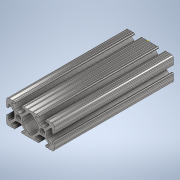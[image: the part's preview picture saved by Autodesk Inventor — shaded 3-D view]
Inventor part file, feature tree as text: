
AUTODESK INVENTOR PART (.ipt)
format: ipt  version: 2020 (Build 240168000, 168)  size: 343,552 bytes
history: native  units: in
note: dims shown in document units (in); Inventor stores cm internally (conversion verified against a paired STEP export)
features: sketch x2, extrude x1
ambient origin geometry x8: Origin, YZ Plane, XZ Plane, XY Plane, X Axis, Y Axis, Z Axis, Center Point
bodies: Solid1 (feature_tree)
feature tree (3):
  extrude  "Extrusion1"  [1 undecoded]
  sketch  "Sketch2"
  sketch  "Sketch1"  dims[d0=5.0in d1=0.0in]
note: 1 required parameter value undecoded (feature->parameter linkage not recoverable at this tier; creation-order binding heuristic only, values carry confidence <= 0.55)
